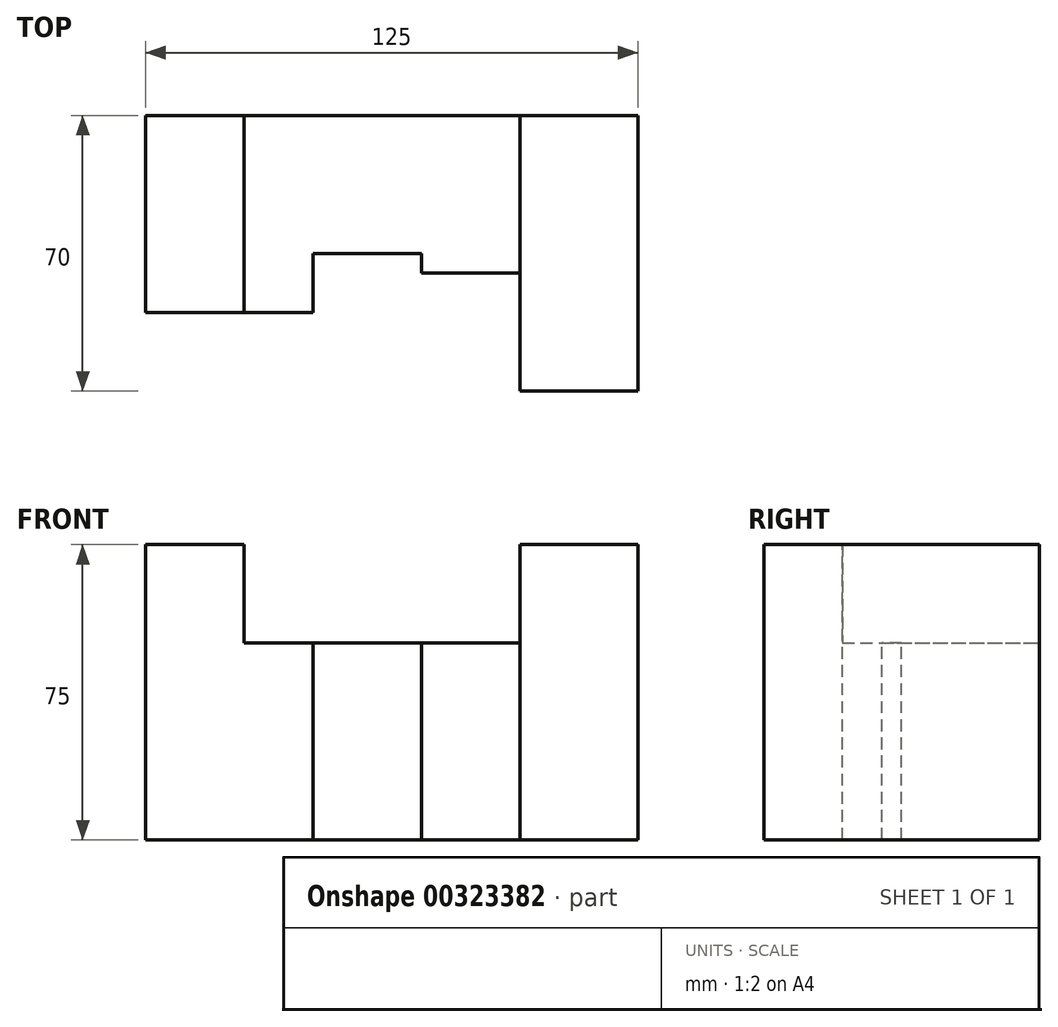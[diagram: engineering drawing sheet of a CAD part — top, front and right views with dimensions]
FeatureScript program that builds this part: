
annotation { "Feature Type Name" : "Feature", "Feature Type Description" : "" }
export const myFeature = defineFeature(function(context is Context, id is Id, definition is map)
    precondition{}
    {
        {
            var Q0;
            Q0=qCreatedBy(makeId("Front.planeOp"),FACE);
            var sketch = newSketch(context, id + "F0", { "sketchPlane" : qUnion([Q0])});
            skLineSegment(sketch, "E0.bottom", {"start": v(-60, 25) * mm, "end": v(65, 25) * mm});
            skLineSegment(sketch, "E0.top", {"start": v(-60, -50) * mm, "end": v(65, -50) * mm});
            skLineSegment(sketch, "E0.left", {"start": v(-60, 25) * mm, "end": v(-60, -50) * mm});
            skLineSegment(sketch, "E0.right", {"start": v(65, 25) * mm, "end": v(65, -50) * mm});
            skLineSegment(sketch, "E1", {"start": v(-35, 25) * mm, "end": v(-35, 0) * mm});
            skLineSegment(sketch, "E2", {"start": v(-35, 0) * mm, "end": v(35, 0) * mm});
            skLineSegment(sketch, "E3", {"start": v(35, 0) * mm, "end": v(35, 25) * mm});
            skSolve(sketch);
        }
        {
            var Q0;
            Q0=makeQuery(id+"F0.imprint","IMPRINT",FACE,{"disambiguationData":[TD([[makeQuery(id+"F0.imprint","IMPRINT",EDGE,{"derivedFrom":sQuery(id+"F0.wireOp",EDGE,"E0.top")}),1.0]])]});
            extrude(context, id + "F1", {"entities" : qUnion([Q0]), "depth" : 70 * mm});
        }
        {
            var Q0;
            {var subQ0=sQuery(id+"F0.wireOp",EDGE,"E0.bottom");Q0=makeQuery(id+"F1.opExtrude","SWEPT_FACE",FACE,{"disambiguationData":[OSD([subQ0]),TDD([makeQuery(id+"F0.imprint","IMPRINT",EDGE,{"disambiguationData":[TD([[makeQuery(id+"F0.imprint","INTERSECT",VERTEX,{"derivedFrom":[subQ0,sQuery(id+"F0.wireOp",EDGE,"E0.right")]}),1.0]])],"derivedFrom":subQ0})])]});}
            var sketch = newSketch(context, id + "F2", { "sketchPlane" : qUnion([Q0])});
            skLineSegment(sketch, "E4", {"start": v(65, 0) * mm, "end": v(-60, 0) * mm});
            skLineSegment(sketch, "E5", {"start": v(-60, 0) * mm, "end": v(-60, -50) * mm});
            skLineSegment(sketch, "E6", {"start": v(45, -40) * mm, "end": v(45, -70) * mm});
            skLineSegment(sketch, "E7", {"start": v(45, -70) * mm, "end": v(65, -70) * mm});
            skLineSegment(sketch, "E8", {"start": v(65, -70) * mm, "end": v(65, 0) * mm});
            skLineSegment(sketch, "E9", {"start": v(-17.5, -50) * mm, "end": v(-17.5, -35) * mm});
            skLineSegment(sketch, "E10", {"start": v(-17.5, -35) * mm, "end": v(10, -35) * mm});
            skLineSegment(sketch, "E11", {"start": v(-60, -50) * mm, "end": v(-17.5, -50) * mm});
            skLineSegment(sketch, "E12", {"start": v(10, -35) * mm, "end": v(10, -40) * mm});
            skLineSegment(sketch, "E13", {"start": v(10, -40) * mm, "end": v(45, -40) * mm});
            skLineSegment(sketch, "E14", {"start": v(-60, -50) * mm, "end": v(-60, -70) * mm});
            skLineSegment(sketch, "E15", {"start": v(-60, -70) * mm, "end": v(45, -70) * mm});
            skSolve(sketch);
        }
        {
            var Q0;
            Q0=makeQuery(id+"F2.imprint","IMPRINT",FACE,{"disambiguationData":[TD([[makeQuery(id+"F2.imprint","IMPRINT",EDGE,{"derivedFrom":sQuery(id+"F2.wireOp",EDGE,"E9")}),-1.0]])]});
            extrude(context, id + "F3", {"entities" : qUnion([Q0]), "operationType" : NewBodyOperationType.REMOVE, "endBound" : BoundingType.THROUGH_ALL, "oppositeDirection" : true, "depth" : 25 * mm});
        }
    });
